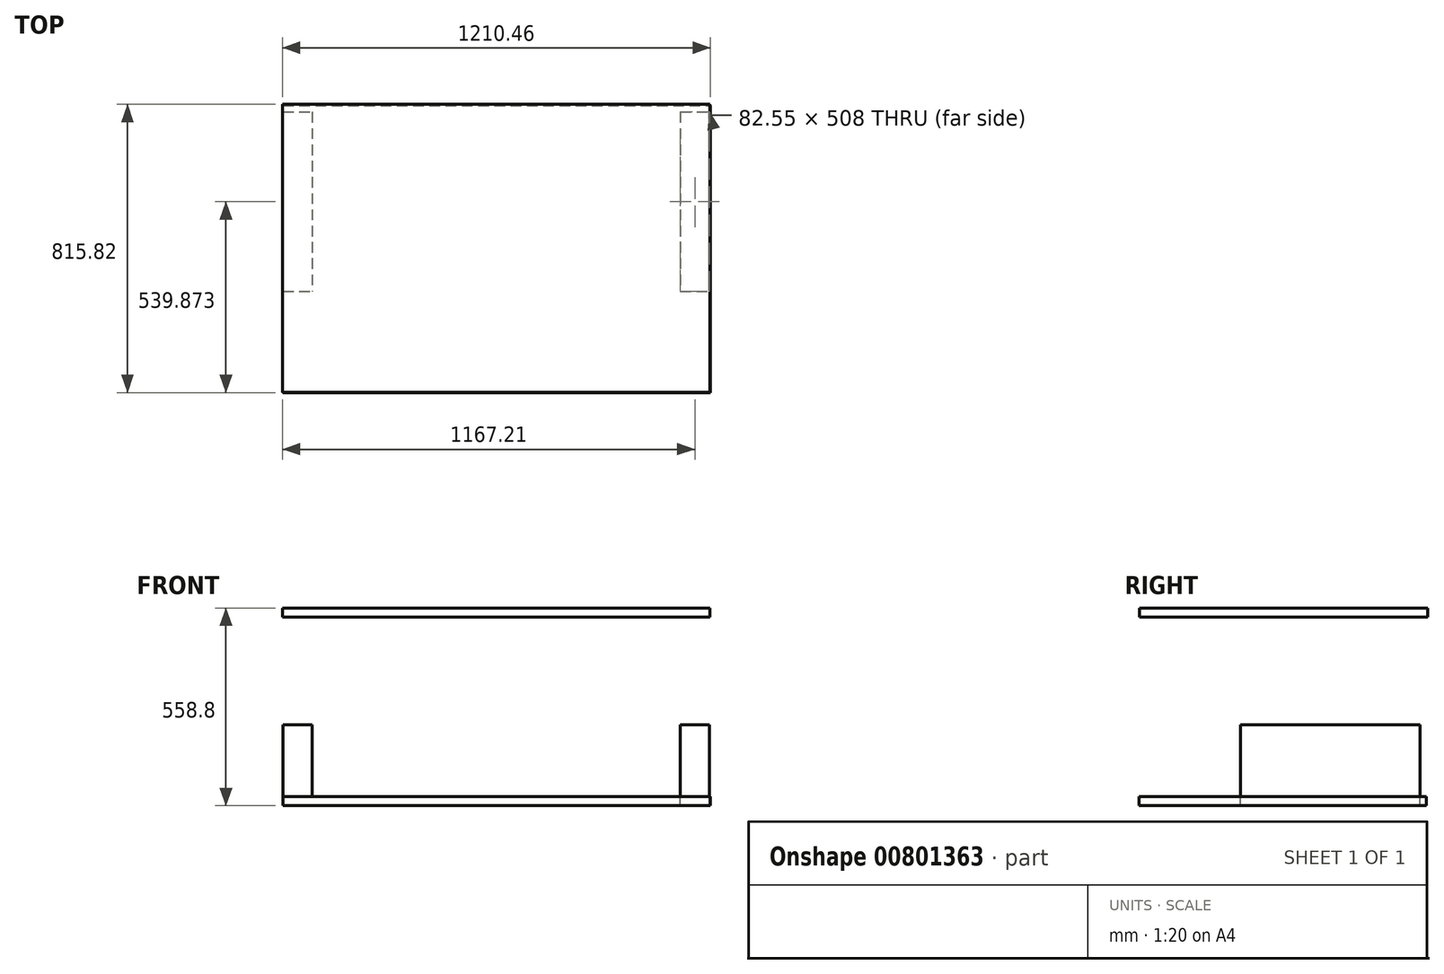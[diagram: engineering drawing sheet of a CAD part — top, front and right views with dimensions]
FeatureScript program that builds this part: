
annotation { "Feature Type Name" : "Feature", "Feature Type Description" : "" }
export const myFeature = defineFeature(function(context is Context, id is Id, definition is map)
    precondition{}
    {
        {
            var Q0;
            Q0=qCreatedBy(makeId("Top.planeOp"),FACE);
            var sketch = newSketch(context, id + "F0", { "sketchPlane" : qUnion([Q0])});
            skLineSegment(sketch, "E0.bottom", {"start": v(-129.3, 477.1) * mm, "end": v(-46.75, 477.1) * mm});
            skLineSegment(sketch, "E0.top", {"start": v(-129.3, -30.9) * mm, "end": v(-46.75, -30.9) * mm});
            skLineSegment(sketch, "E0.left", {"start": v(-129.3, 477.1) * mm, "end": v(-129.3, -30.9) * mm});
            skLineSegment(sketch, "E0.right", {"start": v(-46.75, 477.1) * mm, "end": v(-46.75, -30.9) * mm});
            skLineSegment(sketch, "E1.bottom", {"start": v(994.65, 477.1) * mm, "end": v(1077.2, 477.1) * mm});
            skLineSegment(sketch, "E1.top", {"start": v(994.65, -30.9) * mm, "end": v(1077.2, -30.9) * mm});
            skLineSegment(sketch, "E1.left", {"start": v(994.65, 477.1) * mm, "end": v(994.65, -30.9) * mm});
            skLineSegment(sketch, "E1.right", {"start": v(1077.2, 477.1) * mm, "end": v(1077.2, -30.9) * mm});
            skLineSegment(sketch, "E2.bottom", {"start": v(-129.3, 496.02) * mm, "end": v(1079.18, 496.02) * mm});
            skLineSegment(sketch, "E2.top", {"start": v(-129.3, -316.78) * mm, "end": v(1079.18, -316.78) * mm});
            skLineSegment(sketch, "E2.left", {"start": v(-129.3, 496.02) * mm, "end": v(-129.3, -316.78) * mm});
            skLineSegment(sketch, "E2.right", {"start": v(1079.18, 496.02) * mm, "end": v(1079.18, -316.78) * mm});
            skSolve(sketch);
        }
        {
            var Q0;
            {var subQ0=sQuery(id+"F0.wireOp",EDGE,"E0.bottom");Q0=makeQuery(id+"F0.imprint","IMPRINT",FACE,{"disambiguationData":[TD([[makeQuery(id+"F0.imprint","IMPRINT",EDGE,{"derivedFrom":subQ0}),-1.0]])]});}
            var Q1;
            Q1=makeQuery(id+"F0.imprint","IMPRINT",FACE,{"disambiguationData":[TD([[makeQuery(id+"F0.imprint","IMPRINT",EDGE,{"derivedFrom":sQuery(id+"F0.wireOp",EDGE,"E1.bottom")}),-1.0]])]});
            extrude(context, id + "F1", {"entities" : qUnion([Q0, Q1]), "depth" : 203.2 * mm, "offsetDistance" : 25.4 * mm});
        }
        {
            var Q0;
            Q0 = qSketchRegion(id + "F0", true);
            extrude(context, id + "F2", {"entities" : qUnion([Q0]), "oppositeDirection" : true, "depth" : 25.4 * mm, "offsetDistance" : 25.4 * mm});
        }
        {
            var Q0;
            Q0=makeQuery(id+"F2.opExtrude","CAP_FACE",FACE,{"disambiguationData":[OSD([sQuery(id+"F0.wireOp",EDGE,"E1.bottom"),sQuery(id+"F0.wireOp",EDGE,"E1.top"),sQuery(id+"F0.wireOp",EDGE,"E1.left"),sQuery(id+"F0.wireOp",EDGE,"E1.right"),sQuery(id+"F0.wireOp",EDGE,"E2.bottom"),sQuery(id+"F0.wireOp",EDGE,"E2.top"),sQuery(id+"F0.wireOp",EDGE,"E2.left"),sQuery(id+"F0.wireOp",EDGE,"E2.right")])],"isStart":true});
            cPlane(context, id + "F3", {"entities" : qUnion([Q0]), "cplaneType" : CPlaneType.OFFSET, "offset" : 508 * mm, "width" : 152.4 * mm, "height" : 152.4 * mm});
        }
        {
            var Q0;
            Q0=qCreatedBy(id+"F3.planeOp",FACE);
            var sketch = newSketch(context, id + "F4", { "sketchPlane" : qUnion([Q0])});
            skLineSegment(sketch, "E3.bottom", {"start": v(-131.28, 499.04) * mm, "end": v(1077.64, 499.04) * mm});
            skLineSegment(sketch, "E3.top", {"start": v(-131.28, -316.28) * mm, "end": v(1077.64, -316.28) * mm});
            skLineSegment(sketch, "E3.left", {"start": v(-131.28, 499.04) * mm, "end": v(-131.28, -316.28) * mm});
            skLineSegment(sketch, "E3.right", {"start": v(1077.64, 499.04) * mm, "end": v(1077.64, -316.28) * mm});
            skSolve(sketch);
        }
        {
            var Q0;
            Q0=makeQuery(id+"F4.imprint","IMPRINT",FACE,{"disambiguationData":[TD([[makeQuery(id+"F4.imprint","IMPRINT",EDGE,{"derivedFrom":sQuery(id+"F4.wireOp",EDGE,"E3.bottom")}),-1.0]])]});
            extrude(context, id + "F5", {"entities" : qUnion([Q0]), "depth" : 25.4 * mm, "offsetDistance" : 25.4 * mm});
        }
        {
            var Q0;
            Q0=makeQuery(id+"F2.opExtrude","CAP_FACE",FACE,{"disambiguationData":[OSD([sQuery(id+"F0.wireOp",EDGE,"E1.bottom"),sQuery(id+"F0.wireOp",EDGE,"E1.top"),sQuery(id+"F0.wireOp",EDGE,"E1.left"),sQuery(id+"F0.wireOp",EDGE,"E1.right"),sQuery(id+"F0.wireOp",EDGE,"E2.bottom"),sQuery(id+"F0.wireOp",EDGE,"E2.top"),sQuery(id+"F0.wireOp",EDGE,"E2.left"),sQuery(id+"F0.wireOp",EDGE,"E2.right")])],"isStart":true});
            var sketch = newSketch(context, id + "F6", { "sketchPlane" : qUnion([Q0])});
            skLineSegment(sketch, "E4.bottom", {"start": v(-19.32, 498.75) * mm, "end": v(666.48, 498.75) * mm});
            skLineSegment(sketch, "E4.top", {"start": v(-19.32, -187.05) * mm, "end": v(666.48, -187.05) * mm});
            skLineSegment(sketch, "E4.left", {"start": v(-19.32, 498.75) * mm, "end": v(-19.32, -187.05) * mm});
            skLineSegment(sketch, "E4.right", {"start": v(666.48, 498.75) * mm, "end": v(666.48, -187.05) * mm});
            skLineSegment(sketch, "E5.bottom", {"start": v(1074.03, -114.24) * mm, "end": v(261.23, -114.24) * mm});
            skLineSegment(sketch, "E5.top", {"start": v(1074.03, 495.36) * mm, "end": v(261.23, 495.36) * mm});
            skLineSegment(sketch, "E5.left", {"start": v(1074.03, -114.24) * mm, "end": v(1074.03, 495.36) * mm});
            skLineSegment(sketch, "E5.right", {"start": v(261.23, -114.24) * mm, "end": v(261.23, 495.36) * mm});
            skLineSegment(sketch, "E6.bottom", {"start": v(184.57, 508.14) * mm, "end": v(997.37, 508.14) * mm});
            skLineSegment(sketch, "E6.top", {"start": v(184.57, -304.66) * mm, "end": v(997.37, -304.66) * mm});
            skLineSegment(sketch, "E6.left", {"start": v(184.57, 508.14) * mm, "end": v(184.57, -304.66) * mm});
            skLineSegment(sketch, "E6.right", {"start": v(997.37, 508.14) * mm, "end": v(997.37, -304.66) * mm});
            skSolve(sketch);
        }
    });
